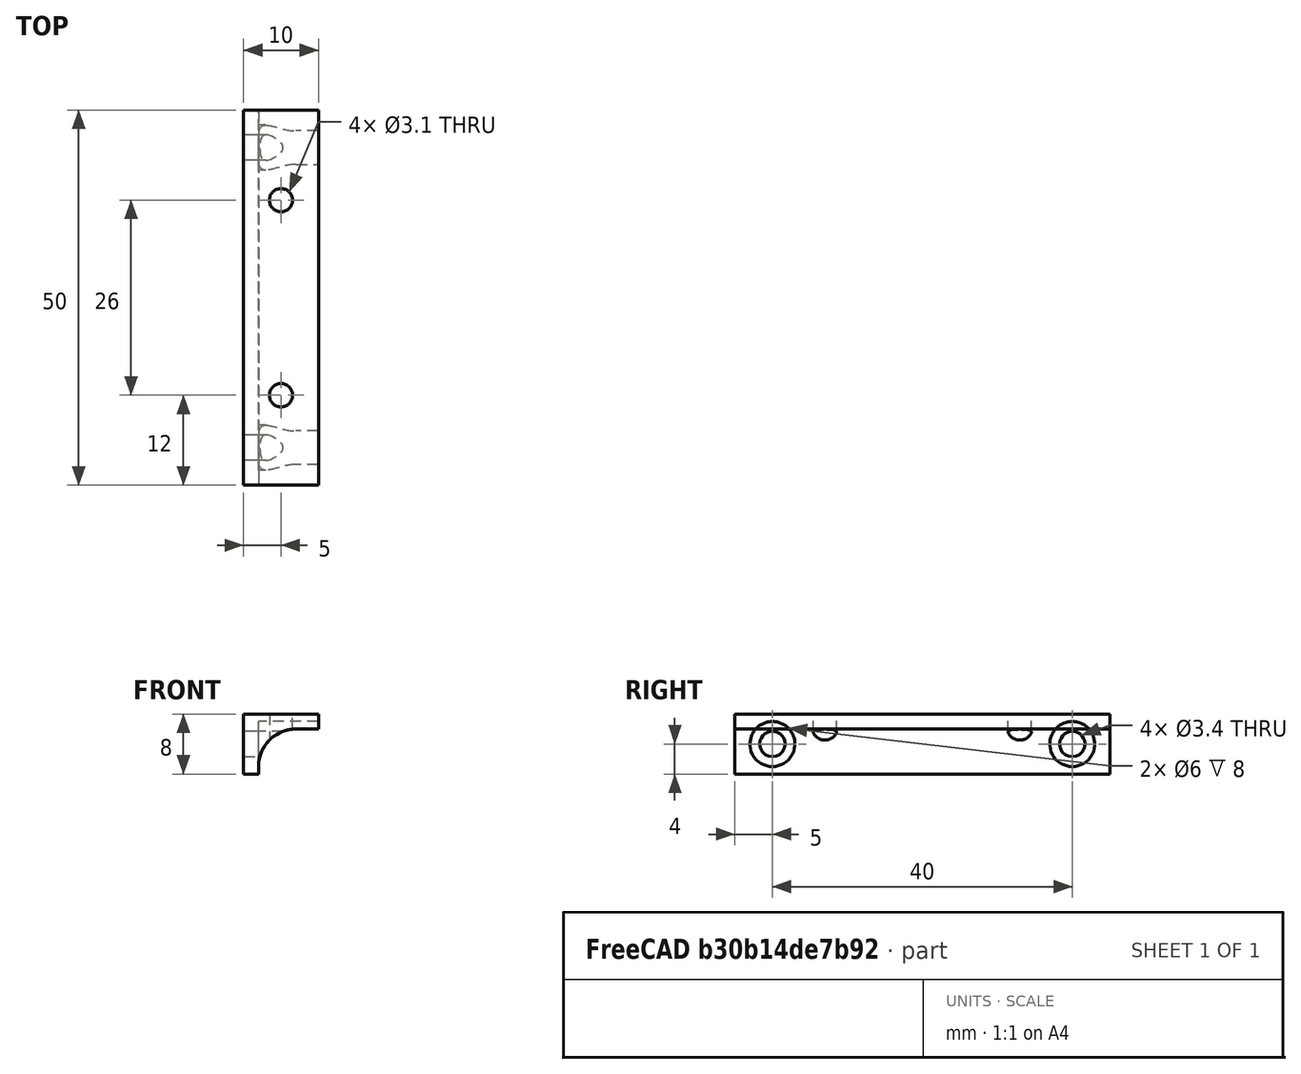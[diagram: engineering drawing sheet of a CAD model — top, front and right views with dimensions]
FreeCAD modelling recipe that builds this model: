
FCSTD DOCUMENT  (FreeCAD 0.20R29603 (Git))
Label: BackplaneSupport
License: All rights reserved
LicenseURL: http://en.wikipedia.org/wiki/All_rights_reserved
objects: Sketcher::SketchObject×4, PartDesign::Pocket×2, Part::Cut×2, PartDesign::Pad×1, Part::Cylinder×1, App::Link×1, PartDesign::Body×1, Part::Feature×1, Mesh::Feature×1
note: 15 computed .brp shape members not serialized (recipe doc carries the construction recipe); baked Part::Feature solids carry a one-line shape summary decoded from their .brp

FEATURE [Sketcher::SketchObject] Sketch
  FullyConstrained = true
  MapMode = 5
  Placement = pos=(0,0,0) rot=(1,0,0;1.5708rad)
  Support = -> [XZ_Plane]
  sketch-geometry (8):
    g0: LineSegment StartX=0 StartY=0 StartZ=0 EndX=0 EndY=8 EndZ=0
    g1: LineSegment StartX=0 StartY=8 StartZ=0 EndX=10 EndY=8 EndZ=0
    g2: LineSegment StartX=10 StartY=8 StartZ=0 EndX=10 EndY=6 EndZ=0
    g3: LineSegment StartX=10 StartY=6 StartZ=0 EndX=7 EndY=6 EndZ=0
    g4: LineSegment StartX=2 StartY=1 StartZ=0 EndX=2 EndY=0 EndZ=0
    g5: LineSegment StartX=2 StartY=0 StartZ=0 EndX=0 EndY=0 EndZ=0
    g6: ArcOfCircle CenterX=7 CenterY=1 CenterZ=0 NormalX=0 NormalY=0 NormalZ=1 AngleXU=0 Radius=5 StartAngle=1.5708 EndAngle=3.14159
    g7: GeomPoint X=2 Y=6 Z=0
  constraints (21):
    c: Coincident(g0,g-1)
    c: PointOnObject(g0,g-2)
    c: Coincident(g1,g0)
    c: Horizontal(g1)
    c: Coincident(g2,g1)
    c: Horizontal(g3)
    c: PointOnObject(g4,g-1)
    c: Vertical(g4)
    c: Coincident(g5,g4)
    c: Coincident(g5,g0)
    c: PointOnObject(g7,g3)
    c: PointOnObject(g7,g4)
    c: Tangent(g3,g6) = -1.5708
    c: Tangent(g4,g6) = -1.5708
    c: DistanceX(g1,g1) = 10
    c: DistanceX(g5,g5) = 2
    c: Coincident(g2,g3)
    c: Vertical(g2)
    c: DistanceY(g0,g0) = 8
    c: DistanceY(g2,g2) = 2
    c: Radius(g6) = 5
FEATURE [PartDesign::Pad] Pad
  Direction = (0,-1,2e-16)
  Length = 50
  Length2 = 10
  Placement = pos=(0,0,0) rot=(1,0,0;1.5708rad)
  Profile = -> Sketch
  ReferenceAxis = -> Sketch [N_Axis]
  Type = 0
FEATURE [Sketcher::SketchObject] Sketch001
  ExternalGeometry = -> [Pad]
  FullyConstrained = true
  MapMode = 5
  Placement = pos=(0,0,0) rot=(0.707107,0,-0.707107;3.14159rad)
  Support = -> [Pad]
  sketch-geometry (2):
    g0: Circle CenterX=-4 CenterY=5 CenterZ=0 NormalX=0 NormalY=0 NormalZ=1 AngleXU=0 Radius=1.7
    g1: Circle CenterX=-4 CenterY=45 CenterZ=0 NormalX=0 NormalY=0 NormalZ=1 AngleXU=0 Radius=1.7
  constraints (6):
    c: Diameter(g0) = 3.4
    c: Diameter(g1) = 3.4
    c: Distance(g0,g-4) = 5
    c: Distance(g1,g-3) = 5
    c: Distance(g0,g-5) = 4
    c: Distance(g1,g-5) = 4
FEATURE [PartDesign::Pocket] Pocket
  BaseFeature = -> Pad
  Direction = (1,0,2e-16)
  Length = 5
  Length2 = 5
  Placement = pos=(0,0,0) rot=(1,0,0;1.5708rad)
  Profile = -> Sketch001
  ReferenceAxis = -> Sketch001 [N_Axis]
  Type = 1
FEATURE [Part::Cylinder] Cylinder
  Angle = 360
  AttacherType = Attacher::AttachEngine3D
  FirstAngle = 0
  Height = 10
  Placement = pos=(2,-45,4) rot=(0,1,0;1.5708rad)
  Radius = 3
  SecondAngle = 0
FEATURE [App::Link] Link  label="Cylinder001"
  LinkPlacement = pos=(2,-5,4) rot=(0,1,0;1.5708rad)
  LinkedObject = -> Cylinder
  Placement = pos=(2,-5,4) rot=(0,1,0;1.5708rad)
FEATURE [Sketcher::SketchObject] Sketch002
  ExternalGeometry = -> [Pocket]
  FullyConstrained = true
  MapMode = 5
  Placement = pos=(0,0,0) rot=(0.707107,0,-0.707107;3.14159rad)
  Support = -> [Pocket]
  sketch-geometry (2):
    g0: Circle CenterX=-4 CenterY=5 CenterZ=0 NormalX=0 NormalY=0 NormalZ=1 AngleXU=0 Radius=3
    g1: Circle CenterX=-4 CenterY=45 CenterZ=0 NormalX=0 NormalY=0 NormalZ=1 AngleXU=0 Radius=3
  constraints (4):
    c: Coincident(g1,g-3)
    c: Coincident(g0,g-6)
    c: Diameter(g0) = 6
    c: Diameter(g1) = 6
FEATURE [Sketcher::SketchObject] Sketch003
  ExternalGeometry = -> [Pocket]
  FullyConstrained = true
  MapMode = 5
  Placement = pos=(0,3.5e-15,8) rot=(0,0,1;3.14159rad)
  Support = -> [Pocket]
  sketch-geometry (2):
    g0: Circle CenterX=-5 CenterY=38 CenterZ=0 NormalX=0 NormalY=0 NormalZ=1 AngleXU=0 Radius=1.55
    g1: Circle CenterX=-5 CenterY=12 CenterZ=0 NormalX=0 NormalY=0 NormalZ=1 AngleXU=0 Radius=1.55
  constraints (6):
    c: Diameter(g0) = 3.1
    c: Diameter(g1) = 3.1
    c: Distance(g0,g-5) = 5
    c: Distance(g1,g-5) = 5
    c: Distance(g1,g-4) = 12
    c: Distance(g0,g-3) = 12
FEATURE [PartDesign::Pocket] Pocket001
  BaseFeature = -> Pocket
  Direction = (0,-2e-16,-1)
  Length = 5
  Length2 = 5
  Placement = pos=(0,0,0) rot=(1,0,0;1.5708rad)
  Profile = -> Sketch003
  ReferenceAxis = -> Sketch003 [N_Axis]
  Type = 1
FEATURE [PartDesign::Body] Body
  Group = -> [Sketch,Pad,Sketch001,Pocket,Sketch002,Sketch003,Pocket001]
  Origin = -> Origin
  Tip = -> Pocket001
FEATURE [Part::Cut] Cut
  Base = -> Pocket001
  Tool = -> Cylinder
FEATURE [Part::Cut] Cut001
  Base = -> Cut
  Tool = -> Link
FEATURE [Part::Feature] Cut001_solid  label="Cut001 (Solid)"
  shape: bbox 10 x 50 x 8 mm, 20 faces (baked)
FEATURE [Mesh::Feature] Mesh  label="Cut001 (Solid) (Meshed)"
